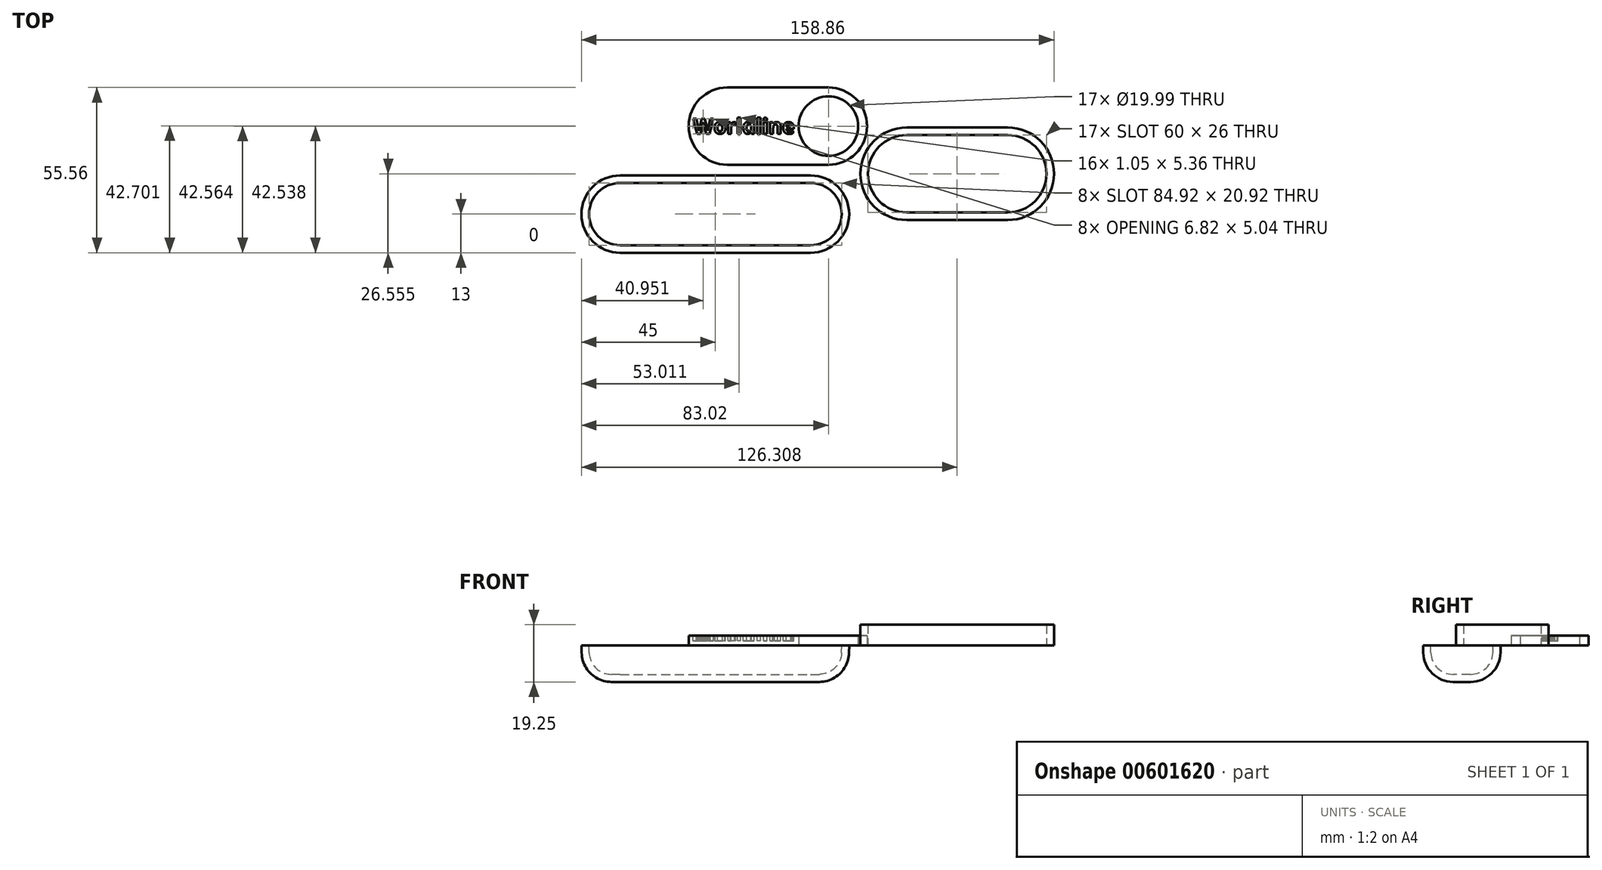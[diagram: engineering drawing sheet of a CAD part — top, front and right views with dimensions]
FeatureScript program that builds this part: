
annotation { "Feature Type Name" : "Feature", "Feature Type Description" : "" }
export const myFeature = defineFeature(function(context is Context, id is Id, definition is map)
    precondition{}
    {
        {
            var Q0;
            Q0=qCreatedBy(makeId("Top.planeOp"),FACE);
            var sketch = newSketch(context, id + "F0", { "sketchPlane" : qUnion([Q0])});
            skLineSegment(sketch, "E0.bottom", {"start": v(0, 0) * mm, "end": v(-90, 0) * mm});
            skLineSegment(sketch, "E0.top", {"start": v(0, -26) * mm, "end": v(-90, -26) * mm});
            skLineSegment(sketch, "E0.left", {"start": v(0, 0) * mm, "end": v(0, -26) * mm});
            skLineSegment(sketch, "E0.right", {"start": v(-90, 0) * mm, "end": v(-90, -26) * mm});
            skCircle(sketch, "E1", {"center": v(-77, -13) * mm, "radius": 13 * mm});
            skCircle(sketch, "E2", {"center": v(-13, -13) * mm, "radius": 13 * mm});
            skSolve(sketch);
        }
        {
            var Q0;
            {var subQ0=sQuery(id+"F0.wireOp",EDGE,"E1");var subQ1=makeQuery(id+"F0.imprint","INTERSECT",VERTEX,{"derivedFrom":[sQuery(id+"F0.wireOp",EDGE,"E0.bottom"),subQ0]});Q0=makeQuery(id+"F0.imprint","IMPRINT",FACE,{"disambiguationData":[TD([[makeQuery(id+"F0.imprint","IMPRINT",EDGE,{"disambiguationData":[TD([[subQ1,-1.0]])],"derivedFrom":subQ0}),1.0]])]});}
            var Q1;
            {var subQ0=sQuery(id+"F0.wireOp",EDGE,"E2");var subQ1=sQuery(id+"F0.wireOp",EDGE,"E0.bottom");var subQ2=makeQuery(id+"F0.imprint","INTERSECT",VERTEX,{"derivedFrom":[subQ1,subQ0]});Q1=makeQuery(id+"F0.imprint","IMPRINT",FACE,{"disambiguationData":[TD([[makeQuery(id+"F0.imprint","IMPRINT",EDGE,{"disambiguationData":[TD([[subQ2,-1.0]])],"derivedFrom":subQ1}),1.0]])]});}
            var Q2;
            {var subQ0=sQuery(id+"F0.wireOp",EDGE,"E2");var subQ1=makeQuery(id+"F0.imprint","INTERSECT",VERTEX,{"derivedFrom":[sQuery(id+"F0.wireOp",EDGE,"E0.bottom"),subQ0]});Q2=makeQuery(id+"F0.imprint","IMPRINT",FACE,{"disambiguationData":[TD([[makeQuery(id+"F0.imprint","IMPRINT",EDGE,{"disambiguationData":[TD([[subQ1,1.0]])],"derivedFrom":subQ0}),1.0]])]});}
            extrude(context, id + "F1", {"entities" : qUnion([Q0, Q1, Q2]), "oppositeDirection" : true, "depth" : 12.2 * mm, "hasDraft" : true, "draftAngle" : 1 * degree, "draftPullDirection" : true});
        }
        {
            var Q0;
            Q0=makeQuery(id+"F1.opExtrude","CAP_FACE",FACE,{"disambiguationData":[OSD([sQuery(id+"F0.wireOp",EDGE,"E0.bottom"),sQuery(id+"F0.wireOp",EDGE,"E0.top"),sQuery(id+"F0.wireOp",EDGE,"E1"),sQuery(id+"F0.wireOp",EDGE,"E2")])],"isStart":false});
            fillet(context, id + "F2", {"entities" : qUnion([Q0]), "radius" : 10 * mm, "tangentPropagation" : true, "allowEdgeOverflow" : false});
        }
        {
            var Q0;
            Q0=qCreatedBy(makeId("Top.planeOp"),FACE);
            var sketch = newSketch(context, id + "F3", { "sketchPlane" : qUnion([Q0])});
            skLineSegment(sketch, "E3.bottom", {"start": v(6.02, 29.56) * mm, "end": v(-53.98, 29.56) * mm});
            skLineSegment(sketch, "E3.top", {"start": v(6.02, 3.56) * mm, "end": v(-53.98, 3.56) * mm});
            skLineSegment(sketch, "E3.left", {"start": v(6.02, 29.56) * mm, "end": v(6.02, 3.56) * mm});
            skLineSegment(sketch, "E3.right", {"start": v(-53.98, 29.56) * mm, "end": v(-53.98, 3.56) * mm});
            skCircle(sketch, "E4", {"center": v(-40.98, 16.56) * mm, "radius": 13 * mm});
            skCircle(sketch, "E5", {"center": v(-6.98, 16.56) * mm, "radius": 13 * mm});
            skCircle(sketch, "E6", {"center": v(-41.18, 16.56) * mm, "radius": 10 * mm});
            skPoint(sketch, "E7", {"position": v(-53.98, 16.56) * mm});
            skLineSegment(sketch, "E8", {"start": v(-53.98, 16.56) * mm, "end": v(-51.18, 16.56) * mm, "construction": true});
            skCircle(sketch, "E9", {"center": v(-6.98, 16.56) * mm, "radius": 10 * mm});
            skSolve(sketch);
        }
        {
            var Q0;
            {var subQ0=sQuery(id+"F3.wireOp",EDGE,"E5");var subQ1=makeQuery(id+"F3.imprint","INTERSECT",VERTEX,{"derivedFrom":[sQuery(id+"F3.wireOp",EDGE,"E3.bottom"),subQ0]});Q0=makeQuery(id+"F3.imprint","IMPRINT",FACE,{"disambiguationData":[TD([[makeQuery(id+"F3.imprint","IMPRINT",EDGE,{"disambiguationData":[TD([[subQ1,1.0]])],"derivedFrom":subQ0}),1.0]])]});}
            var Q1;
            {var subQ0=sQuery(id+"F3.wireOp",EDGE,"E5");var subQ1=sQuery(id+"F3.wireOp",EDGE,"E3.bottom");var subQ2=makeQuery(id+"F3.imprint","INTERSECT",VERTEX,{"derivedFrom":[subQ1,subQ0]});Q1=makeQuery(id+"F3.imprint","IMPRINT",FACE,{"disambiguationData":[TD([[makeQuery(id+"F3.imprint","IMPRINT",EDGE,{"disambiguationData":[TD([[subQ2,-1.0]])],"derivedFrom":subQ1}),1.0]])]});}
            var Q2;
            Q2=makeQuery(id+"F3.imprint","IMPRINT",FACE,{"disambiguationData":[TD([[makeQuery(id+"F3.imprint","IMPRINT",EDGE,{"derivedFrom":sQuery(id+"F3.wireOp",EDGE,"a6fba586-438c-4d96-be7d-434e70076c33.sketch_text.stroke-20")}),1.0]])]});
            var Q3;
            Q3=makeQuery(id+"F3.imprint","IMPRINT",FACE,{"disambiguationData":[TD([[makeQuery(id+"F3.imprint","IMPRINT",EDGE,{"derivedFrom":sQuery(id+"F3.wireOp",EDGE,"a6fba586-438c-4d96-be7d-434e70076c33.sketch_text.stroke-0")}),1.0]])]});
            var Q4;
            Q4=makeQuery(id+"F3.imprint","IMPRINT",FACE,{"disambiguationData":[TD([[makeQuery(id+"F3.imprint","IMPRINT",EDGE,{"derivedFrom":sQuery(id+"F3.wireOp",EDGE,"E6")}),-1.0]])]});
            var Q5;
            Q5=makeQuery(id+"F3.imprint","IMPRINT",FACE,{"disambiguationData":[TD([[makeQuery(id+"F3.imprint","IMPRINT",EDGE,{"derivedFrom":sQuery(id+"F3.wireOp",EDGE,"f5b48d19-ef08-4ac2-a32c-5731788e0d77.sketch_text.stroke-82")}),1.0]])]});
            var Q6;
            {var subQ0=sQuery(id+"F3.wireOp",EDGE,"f5b48d19-ef08-4ac2-a32c-5731788e0d77.sketch_text.stroke-125");Q6=makeQuery(id+"F3.imprint","IMPRINT",FACE,{"disambiguationData":[TD([[makeQuery(id+"F3.imprint","IMPRINT",EDGE,{"derivedFrom":subQ0}),1.0]])]});}
            var Q7;
            Q7=makeQuery(id+"F3.imprint","IMPRINT",FACE,{"disambiguationData":[TD([[makeQuery(id+"F3.imprint","IMPRINT",EDGE,{"derivedFrom":sQuery(id+"F3.wireOp",EDGE,"f5b48d19-ef08-4ac2-a32c-5731788e0d77.sketch_text.stroke-0")}),1.0]])]});
            var Q8;
            {var subQ5=sQuery(id+"F3.wireOp",EDGE,"f5b48d19-ef08-4ac2-a32c-5731788e0d77.sketch_text.stroke-86");Q8=makeQuery(id+"F3.imprint","IMPRINT",FACE,{"disambiguationData":[TD([[makeQuery(id+"F3.imprint","IMPRINT",EDGE,{"derivedFrom":subQ5}),-1.0]])]});}
            var Q9;
            {var subQ5=sQuery(id+"F3.wireOp",EDGE,"f5b48d19-ef08-4ac2-a32c-5731788e0d77.sketch_text.stroke-88");Q9=makeQuery(id+"F3.imprint","IMPRINT",FACE,{"disambiguationData":[TD([[makeQuery(id+"F3.imprint","IMPRINT",EDGE,{"derivedFrom":subQ5}),-1.0]])]});}
            var Q10;
            Q10=makeQuery(id+"F3.imprint","IMPRINT",FACE,{"disambiguationData":[TD([[makeQuery(id+"F3.imprint","IMPRINT",EDGE,{"derivedFrom":sQuery(id+"F3.wireOp",EDGE,"E6")}),1.0]])]});
            extrude(context, id + "F4", {"entities" : qUnion([Q0, Q1, Q2, Q3, Q4, Q5, Q6, Q7, Q8, Q9, Q10]), "depth" : 3.4 * mm});
        }
        {
            var Q0;
            Q0=makeQuery(id+"F1.opExtrude","CAP_FACE",FACE,{"disambiguationData":[OSD([sQuery(id+"F0.wireOp",EDGE,"E0.bottom"),sQuery(id+"F0.wireOp",EDGE,"E0.top"),sQuery(id+"F0.wireOp",EDGE,"E1"),sQuery(id+"F0.wireOp",EDGE,"E2")])],"isStart":true});
            shell(context, id + "F5", {"entities" : qUnion([Q0]), "thickness" : 2.54 * mm});
        }
        {
            var Q0;
            Q0=qCreatedBy(makeId("Top.planeOp"),FACE);
            var sketch = newSketch(context, id + "F6", { "sketchPlane" : qUnion([Q0])});
            skLineSegment(sketch, "E10.bottom", {"start": v(53.3, 13.56) * mm, "end": v(19.3, 13.56) * mm});
            skLineSegment(sketch, "E10.top", {"start": v(53.3, -12.44) * mm, "end": v(19.3, -12.44) * mm});
            skArc(sketch, "E11", {"start": v(19.3, 13.56) * mm, "mid": v(6.3, 0.56) * mm, "end": v(19.3, -12.44) * mm});
            skArc(sketch, "E12", {"start": v(53.3, -12.44) * mm, "mid": v(66.3, 0.56) * mm, "end": v(53.3, 13.56) * mm});
            skLineSegment(sketch, "E13.0", {"start": v(53.3, 16.1) * mm, "end": v(19.3, 16.1) * mm});
            skArc(sketch, "E13.1", {"start": v(53.3, -15) * mm, "mid": v(68.86, 0.56) * mm, "end": v(53.3, 16.1) * mm});
            skLineSegment(sketch, "E13.2", {"start": v(53.3, -15) * mm, "end": v(19.3, -15) * mm});
            skArc(sketch, "E13.3", {"start": v(19.3, 16.1) * mm, "mid": v(3.76, 0.56) * mm, "end": v(19.3, -15) * mm});
            skSolve(sketch);
        }
        {
            var Q0;
            Q0=makeQuery(id+"F6.imprint","IMPRINT",FACE,{"disambiguationData":[TD([[makeQuery(id+"F6.imprint","IMPRINT",EDGE,{"derivedFrom":sQuery(id+"F6.wireOp",EDGE,"E10.bottom")}),-1.0]])]});
            extrude(context, id + "F7", {"entities" : qUnion([Q0]), "depth" : 7.05 * mm});
        }
        {
            var Q0;
            Q0=makeQuery(id+"F4.opExtrude","CAP_FACE",FACE,{"disambiguationData":[OSD([sQuery(id+"F3.wireOp",EDGE,"E3.bottom"),sQuery(id+"F3.wireOp",EDGE,"E3.top"),sQuery(id+"F3.wireOp",EDGE,"E4"),sQuery(id+"F3.wireOp",EDGE,"E5"),sQuery(id+"F3.wireOp",EDGE,"E9")])],"isStart":false});
            var sketch = newSketch(context, id + "F8", { "sketchPlane" : qUnion([Q0])});
            skText(sketch, "E14", { "text": "Worldline", "fontName": "OpenSans-Bold.ttf"});
            const initialGuessF8  = {"E14": [-0.05246, 0.01402, 1, 0, 0.00508]};
            skSetInitialGuess(sketch, initialGuessF8);
            skSolve(sketch);
        }
        {
            var Q0;
            Q0=qSketchRegion(id+"F8",true);
            extrude(context, id + "F9", {"entities" : qUnion([Q0]), "operationType" : NewBodyOperationType.REMOVE, "oppositeDirection" : true, "depth" : 1.78 * mm});
        }
    });
